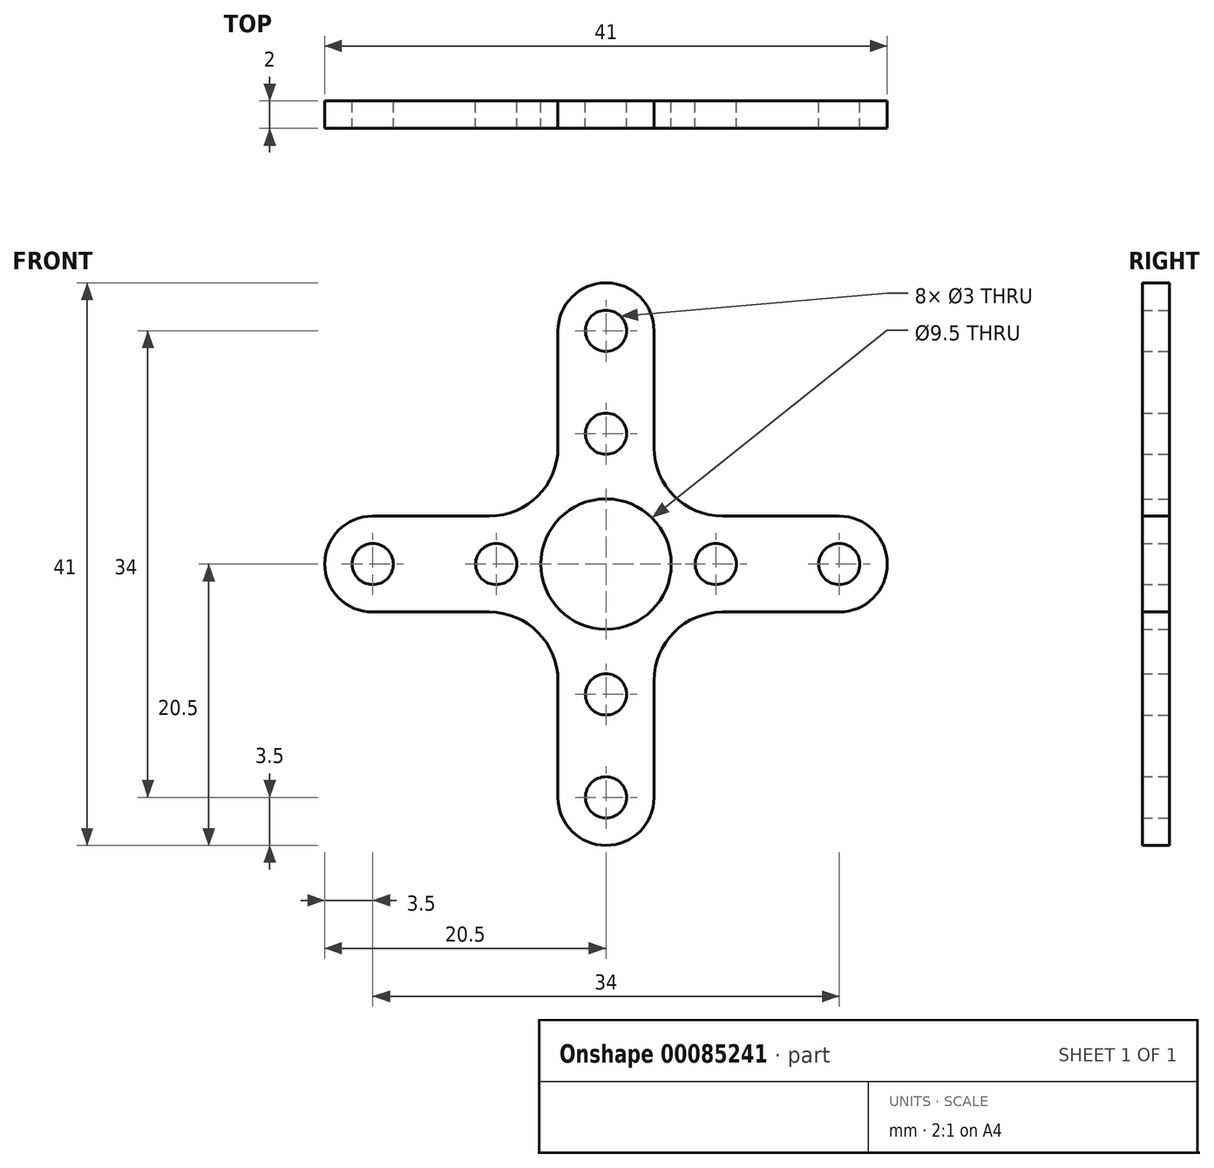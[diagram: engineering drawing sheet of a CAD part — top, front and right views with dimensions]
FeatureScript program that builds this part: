
annotation { "Feature Type Name" : "Feature", "Feature Type Description" : "" }
export const myFeature = defineFeature(function(context is Context, id is Id, definition is map)
    precondition{}
    {
        {
            var Q0;
            Q0=qCreatedBy(makeId("Front.planeOp"),FACE);
            var sketch = newSketch(context, id + "F0", { "sketchPlane" : qUnion([Q0])});
            skLineSegment(sketch, "E0", {"start": v(-17, 3.5) * mm, "end": v(-8.5, 3.5) * mm});
            skArc(sketch, "E1", {"start": v(-8.5, 3.5) * mm, "mid": v(-4.96, 4.96) * mm, "end": v(-3.5, 8.5) * mm});
            skLineSegment(sketch, "E2", {"start": v(-3.5, 8.5) * mm, "end": v(-3.5, 17) * mm});
            skArc(sketch, "E3.1.0", {"start": v(-3.5, -8.5) * mm, "mid": v(-4.96, -4.96) * mm, "end": v(-8.5, -3.5) * mm});
            skLineSegment(sketch, "E3.1.1", {"start": v(-8.5, -3.5) * mm, "end": v(-17, -3.5) * mm});
            skLineSegment(sketch, "E3.1.2", {"start": v(-3.5, -17) * mm, "end": v(-3.5, -8.5) * mm});
            skArc(sketch, "E3.2.0", {"start": v(8.5, -3.5) * mm, "mid": v(4.96, -4.96) * mm, "end": v(3.5, -8.5) * mm});
            skLineSegment(sketch, "E3.2.1", {"start": v(3.5, -8.5) * mm, "end": v(3.5, -17) * mm});
            skLineSegment(sketch, "E3.2.2", {"start": v(17, -3.5) * mm, "end": v(8.5, -3.5) * mm});
            skArc(sketch, "E3.3.0", {"start": v(3.5, 8.5) * mm, "mid": v(4.96, 4.96) * mm, "end": v(8.5, 3.5) * mm});
            skLineSegment(sketch, "E3.3.1", {"start": v(8.5, 3.5) * mm, "end": v(17, 3.5) * mm});
            skLineSegment(sketch, "E3.3.2", {"start": v(3.5, 17) * mm, "end": v(3.5, 8.5) * mm});
            skPoint(sketch, "E3.center", {"position": v(0, 0) * mm});
            skArc(sketch, "E4", {"start": v(3.5, 17) * mm, "mid": v(0, 20.5) * mm, "end": v(-3.5, 17) * mm});
            skArc(sketch, "E5", {"start": v(17, -3.5) * mm, "mid": v(20.5, 0) * mm, "end": v(17, 3.5) * mm});
            skArc(sketch, "E6", {"start": v(-3.5, -17) * mm, "mid": v(0, -20.5) * mm, "end": v(3.5, -17) * mm});
            skArc(sketch, "E7", {"start": v(-17, 3.5) * mm, "mid": v(-20.5, 0) * mm, "end": v(-17, -3.5) * mm});
            skCircle(sketch, "E8", {"center": v(0, 0) * mm, "radius": 4.75 * mm});
            skCircle(sketch, "E9", {"center": v(-17, 0) * mm, "radius": 1.5 * mm});
            skCircle(sketch, "E10", {"center": v(17, 0) * mm, "radius": 1.5 * mm});
            skCircle(sketch, "E11", {"center": v(0, 17) * mm, "radius": 1.5 * mm});
            skCircle(sketch, "E12", {"center": v(0, -17) * mm, "radius": 1.5 * mm});
            skCircle(sketch, "E13", {"center": v(-8, 0) * mm, "radius": 1.5 * mm});
            skCircle(sketch, "E14", {"center": v(0, 9.5) * mm, "radius": 1.5 * mm});
            skCircle(sketch, "E15", {"center": v(8, 0) * mm, "radius": 1.5 * mm});
            skCircle(sketch, "E16", {"center": v(0, -9.5) * mm, "radius": 1.5 * mm});
            skCircle(sketch, "E17", {"center": v(0, 0) * mm, "radius": 8 * mm, "construction": true});
            skCircle(sketch, "E18", {"center": v(0, 0) * mm, "radius": 9.5 * mm, "construction": true});
            skSolve(sketch);
        }
        {
            var Q0;
            Q0 = qSketchRegion(id + "F0", true);
            extrude(context, id + "F1", {"entities" : qUnion([Q0]), "depth" : 2 * mm});
        }
    });
